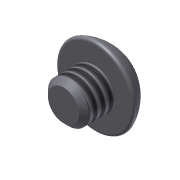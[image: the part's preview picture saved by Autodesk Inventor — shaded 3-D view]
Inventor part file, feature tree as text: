
AUTODESK INVENTOR PART (.ipt)
format: ipt  version: 2013 (Build 170138000, 138)  size: 132,608 bytes
history: native  units: in
note: dims shown in document units (in); Inventor stores cm internally (conversion verified against a paired STEP export)
features: sketch x3, extrude x2, revolve x1, chamfer x1, thread x1
ambient origin geometry x8: Origin, YZ Plane, XZ Plane, XY Plane, X Axis, Y Axis, Z Axis, Center Point
bodies: Solid1 (feature_tree)
feature tree (8):
  extrude  "Extrusion1"  Depth=0.125in TaperAngle=0.0deg
  revolve  "Revolution1"  [1 undecoded]
  extrude  "Extrusion2"  Depth=0.0938in
  chamfer  "Chamfer1"  Distance=0.0625in
  thread  "Thread1"  [1 undecoded]
  sketch  "Sketch1"  dims[d0=0.164in d1=0.125in d2=0.0in]
  sketch  "Sketch2"  dims[d3=0.087in d6=0.09in]
  sketch  "Sketch3"  dims[d7=90.0deg d8=0.0938in d9=0.0625in d10=0.0in d12=0.156in d13=0.02in d14=0.125in d15=45.0deg d16=1.0in d17=0.0in]
note: 2 required parameter values undecoded (feature->parameter linkage not recoverable at this tier; creation-order binding heuristic only, values carry confidence <= 0.55)